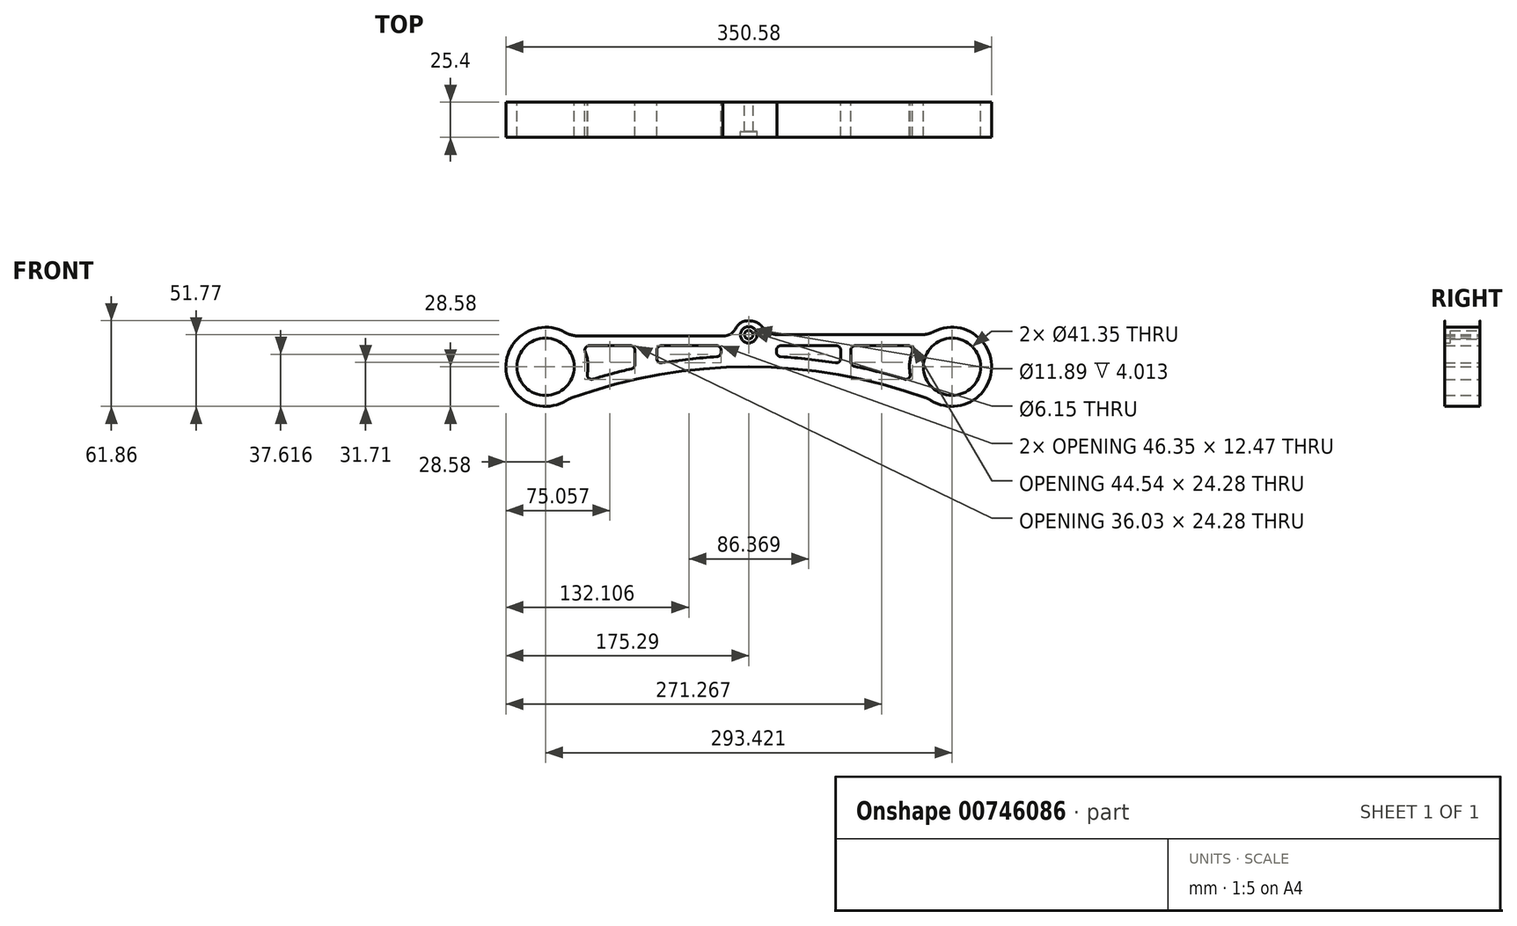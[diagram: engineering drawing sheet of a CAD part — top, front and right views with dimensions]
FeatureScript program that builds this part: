
annotation { "Feature Type Name" : "Feature", "Feature Type Description" : "" }
export const myFeature = defineFeature(function(context is Context, id is Id, definition is map)
    precondition{}
    {
        {
            var Q0;
            Q0=qCreatedBy(makeId("Front.planeOp"),FACE);
            var sketch = newSketch(context, id + "F0", { "sketchPlane" : qUnion([Q0])});
            skCircle(sketch, "E0", {"center": v(0, 0) * mm, "radius": 20.68 * mm});
            skCircle(sketch, "E1", {"center": v(293.42, 0) * mm, "radius": 20.68 * mm});
            skCircle(sketch, "E2", {"center": v(146.71, 23.2) * mm, "radius": 3.07 * mm});
            skLineSegment(sketch, "E3", {"start": v(167.05, 23.27) * mm, "end": v(271.58, 23.27) * mm});
            skArc(sketch, "E4", {"start": v(280.32, 25.4) * mm, "mid": v(321.97, -1.13) * mm, "end": v(278.35, -24.28) * mm});
            skFitSpline(sketch, "E5", {"points": [v(146.71, 33.28) * mm, v(167.05, 23.27) * mm], "startDerivative": vector(34.5, 0) * mm, "endDerivative": vector(33.63, -0.52) * mm});
            skArc(sketch, "E6", {"start": v(274.8, -22.56) * mm, "mid": v(211.74, -5.68) * mm, "end": v(146.71, 0) * mm});
            skCircle(sketch, "E7", {"center": v(146.71, 23.2) * mm, "radius": 5.94 * mm});
            skPoint(sketch, "E8.visualSharp", {"position": v(276.84, 23.27) * mm});
            skArc(sketch, "E8.filletArc", {"start": v(271.58, 23.27) * mm, "mid": v(276.08, 23.8) * mm, "end": v(280.32, 25.4) * mm});
            skPoint(sketch, "E9.visualSharp", {"position": v(276.93, -23.33) * mm});
            skArc(sketch, "E9.filletArc", {"start": v(278.35, -24.28) * mm, "mid": v(276.62, -23.33) * mm, "end": v(274.8, -22.56) * mm});
            skArc(sketch, "E10", {"start": v(264.77, 10.96) * mm, "mid": v(262.89, 2.94) * mm, "end": v(263.2, -5.3) * mm});
            skLineSegment(sketch, "E11", {"start": v(261.8, 15.27) * mm, "end": v(223.6, 15.27) * mm});
            skArc(sketch, "E12.filletArc", {"start": v(264.77, 10.96) * mm, "mid": v(264.42, 13.9) * mm, "end": v(261.8, 15.27) * mm});
            skArc(sketch, "E13.filletArc", {"start": v(259.15, -8.88) * mm, "mid": v(262.18, -8.22) * mm, "end": v(263.2, -5.3) * mm});
            skFitSpline(sketch, "E14.MirrorCS", {"points": [v(146.71, 33.28) * mm, v(128.16, 22.3) * mm], "startDerivative": vector(-34.5, 0) * mm, "endDerivative": vector(-33.63, -0.52) * mm});
            skLineSegment(sketch, "E15.MirrorCS", {"start": v(128.16, 22.3) * mm, "end": v(23.63, 22.3) * mm});
            skArc(sketch, "E16.MirrorCS", {"start": v(14.18, 24.8) * mm, "mid": v(-28.57, -0.52) * mm, "end": v(15.07, -24.28) * mm});
            skArc(sketch, "E17.MirrorCS", {"start": v(15.07, -24.28) * mm, "mid": v(16.8, -23.33) * mm, "end": v(18.61, -22.56) * mm});
            skArc(sketch, "E18.MirrorCS", {"start": v(23.63, 22.3) * mm, "mid": v(18.74, 22.94) * mm, "end": v(14.18, 24.8) * mm});
            skArc(sketch, "E19.MirrorCS", {"start": v(18.61, -22.56) * mm, "mid": v(81.68, -5.68) * mm, "end": v(146.71, 0) * mm});
            skArc(sketch, "E20", {"start": v(209.38, 2.84) * mm, "mid": v(189.6, 5.6) * mm, "end": v(169.7, 7.3) * mm});
            skLineSegment(sketch, "E21", {"start": v(213.07, 12.1) * mm, "end": v(213.07, 5.97) * mm});
            skLineSegment(sketch, "E22", {"start": v(209.9, 15.27) * mm, "end": v(169.9, 15.27) * mm});
            skLineSegment(sketch, "E23", {"start": v(166.72, 12.1) * mm, "end": v(166.72, 10.48) * mm});
            skPoint(sketch, "E24.visualSharp", {"position": v(166.72, 7.48) * mm});
            skArc(sketch, "E24.filletArc", {"start": v(166.72, 10.48) * mm, "mid": v(167.58, 8.3) * mm, "end": v(169.7, 7.3) * mm});
            skPoint(sketch, "E25.visualSharp", {"position": v(166.72, 15.27) * mm});
            skArc(sketch, "E25.filletArc", {"start": v(169.9, 15.27) * mm, "mid": v(167.65, 14.34) * mm, "end": v(166.72, 12.1) * mm});
            skPoint(sketch, "E26.visualSharp", {"position": v(213.07, 15.27) * mm});
            skArc(sketch, "E26.filletArc", {"start": v(213.07, 12.1) * mm, "mid": v(212.14, 14.34) * mm, "end": v(209.9, 15.27) * mm});
            skPoint(sketch, "E27.visualSharp", {"position": v(213.07, 2.2) * mm});
            skArc(sketch, "E27.filletArc", {"start": v(209.38, 2.84) * mm, "mid": v(211.95, 3.55) * mm, "end": v(213.07, 5.97) * mm});
            skArc(sketch, "E28.MirrorCS", {"start": v(123.53, 15.27) * mm, "mid": v(125.77, 14.34) * mm, "end": v(126.7, 12.1) * mm});
            skLineSegment(sketch, "E29.MirrorCS", {"start": v(126.7, 12.1) * mm, "end": v(126.7, 10.48) * mm});
            skArc(sketch, "E30.MirrorCS", {"start": v(126.7, 10.48) * mm, "mid": v(125.84, 8.3) * mm, "end": v(123.72, 7.3) * mm});
            skArc(sketch, "E31.MirrorCS", {"start": v(84.04, 2.84) * mm, "mid": v(103.82, 5.6) * mm, "end": v(123.72, 7.3) * mm});
            skArc(sketch, "E32.MirrorCS", {"start": v(84.04, 2.84) * mm, "mid": v(81.47, 3.55) * mm, "end": v(80.35, 5.97) * mm});
            skLineSegment(sketch, "E33.MirrorCS", {"start": v(80.35, 12.1) * mm, "end": v(80.35, 5.97) * mm});
            skArc(sketch, "E34.MirrorCS", {"start": v(80.35, 12.1) * mm, "mid": v(81.28, 14.34) * mm, "end": v(83.53, 15.27) * mm});
            skLineSegment(sketch, "E35.MirrorCS", {"start": v(83.53, 15.27) * mm, "end": v(123.53, 15.27) * mm});
            skArc(sketch, "E36", {"start": v(259.15, -8.88) * mm, "mid": v(241.16, -3.83) * mm, "end": v(222.96, 0.33) * mm});
            skLineSegment(sketch, "E37", {"start": v(220.42, 12.1) * mm, "end": v(220.42, 3.45) * mm});
            skPoint(sketch, "E38.visualSharp", {"position": v(220.42, 15.27) * mm});
            skArc(sketch, "E38.filletArc", {"start": v(223.6, 15.27) * mm, "mid": v(221.35, 14.34) * mm, "end": v(220.42, 12.1) * mm});
            skPoint(sketch, "E39.visualSharp", {"position": v(220.42, 0.84) * mm});
            skArc(sketch, "E39.filletArc", {"start": v(220.42, 3.45) * mm, "mid": v(221.13, 1.44) * mm, "end": v(222.96, 0.33) * mm});
            skLineSegment(sketch, "E40.MirrorCS", {"start": v(64.5, 12.1) * mm, "end": v(64.5, 1.62) * mm});
            skLineSegment(sketch, "E41.MirrorCS", {"start": v(31.62, 15.27) * mm, "end": v(61.32, 15.27) * mm});
            skArc(sketch, "E42.MirrorCS", {"start": v(28.65, 10.96) * mm, "mid": v(30.53, 2.94) * mm, "end": v(30.22, -5.3) * mm});
            skArc(sketch, "E43.MirrorCS", {"start": v(34.28, -8.88) * mm, "mid": v(31.24, -8.22) * mm, "end": v(30.22, -5.3) * mm});
            skArc(sketch, "E44.MirrorCS", {"start": v(34.28, -8.88) * mm, "mid": v(48.08, -4.92) * mm, "end": v(62.02, -1.48) * mm});
            skArc(sketch, "E45.MirrorCS", {"start": v(64.5, 1.62) * mm, "mid": v(63.8, -0.37) * mm, "end": v(62.02, -1.48) * mm});
            skArc(sketch, "E46.MirrorCS", {"start": v(61.32, 15.27) * mm, "mid": v(63.56, 14.34) * mm, "end": v(64.5, 12.1) * mm});
            skArc(sketch, "E47.MirrorCS", {"start": v(28.65, 10.96) * mm, "mid": v(29, 13.9) * mm, "end": v(31.62, 15.27) * mm});
            skLineSegment(sketch, "E48", {"start": v(146.71, 33.28) * mm, "end": v(146.71, 23.2) * mm, "construction": true});
            skLineSegment(sketch, "E49", {"start": v(146.71, 23.2) * mm, "end": v(146.71, 0) * mm, "construction": true});
            skLineSegment(sketch, "E50", {"start": v(31.62, 15.27) * mm, "end": v(261.8, 15.27) * mm, "construction": true});
            skSolve(sketch);
        }
        {
            var Q0;
            Q0=makeQuery(id+"F0.imprint","IMPRINT",FACE,{"disambiguationData":[TD([[makeQuery(id+"F0.imprint","IMPRINT",EDGE,{"derivedFrom":sQuery(id+"F0.wireOp",EDGE,"E0")}),-1.0]])]});
            extrude(context, id + "F1", {"entities" : qUnion([Q0]), "depth" : 25.4 * mm, "offsetDistance" : 25.4 * mm});
        }
        {
            var Q0;
            Q0=makeQuery(id+"F0.imprint","IMPRINT",FACE,{"disambiguationData":[TD([[makeQuery(id+"F0.imprint","IMPRINT",EDGE,{"derivedFrom":sQuery(id+"F0.wireOp",EDGE,"E2")}),-1.0]])]});
            extrude(context, id + "F2", {"entities" : qUnion([Q0]), "operationType" : NewBodyOperationType.ADD, "depth" : 21.4 * mm, "offsetDistance" : 25.4 * mm});
        }
    });
